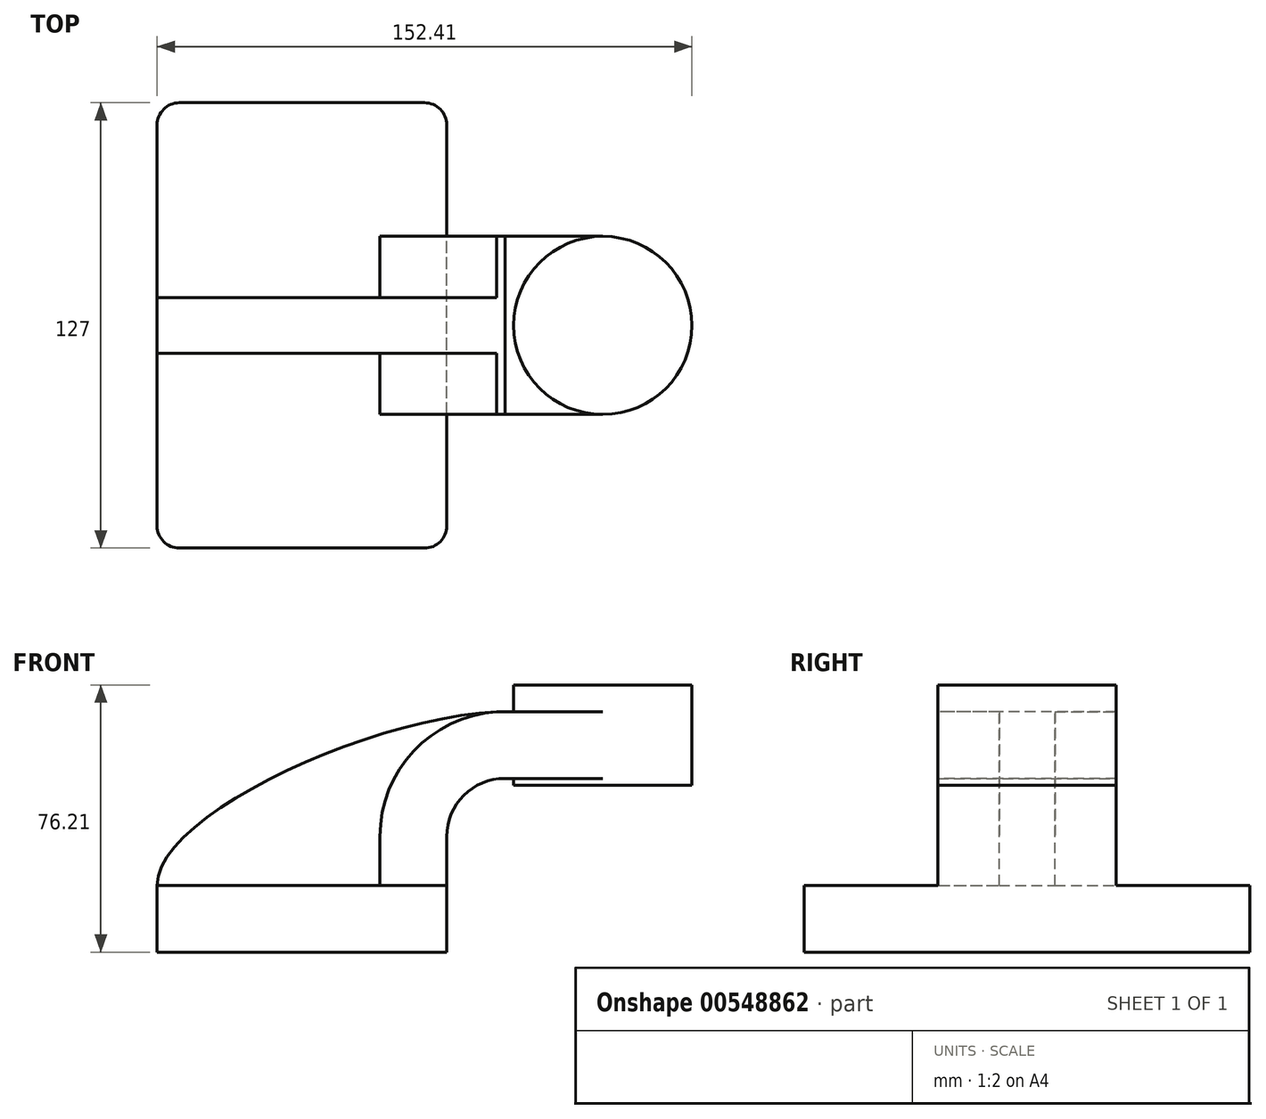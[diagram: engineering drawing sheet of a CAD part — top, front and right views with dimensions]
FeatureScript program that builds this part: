
annotation { "Feature Type Name" : "Feature", "Feature Type Description" : "" }
export const myFeature = defineFeature(function(context is Context, id is Id, definition is map)
    precondition{}
    {
        {
            var Q0;
            Q0=qCreatedBy(makeId("Front.planeOp"),FACE);
            var sketch = newSketch(context, id + "F0", { "sketchPlane" : qUnion([Q0])});
            skLineSegment(sketch, "E0.bottom", {"start": v(41.28, -9.53) * mm, "end": v(-41.28, -9.53) * mm});
            skLineSegment(sketch, "E0.top", {"start": v(41.28, 9.53) * mm, "end": v(-41.28, 9.52) * mm});
            skLineSegment(sketch, "E0.left", {"start": v(41.28, -9.53) * mm, "end": v(41.28, 9.53) * mm});
            skLineSegment(sketch, "E0.right", {"start": v(-41.28, -9.53) * mm, "end": v(-41.28, 9.52) * mm});
            skPoint(sketch, "E0.middle", {"position": v(0, 0) * mm});
            skLineSegment(sketch, "E1.left", {"start": v(3.55, 33.58) * mm, "end": v(3.55, 33.58) * mm});
            skLineSegment(sketch, "E1.right", {"start": v(63.14, 33.58) * mm, "end": v(63.14, 33.58) * mm});
            skPoint(sketch, "E1.middle", {"position": v(33.35, 33.58) * mm});
            skLineSegment(sketch, "E2", {"start": v(41.28, 9.53) * mm, "end": v(41.28, 23.44) * mm});
            skArc(sketch, "E3", {"start": v(41.28, 23.44) * mm, "mid": v(46.13, 35.15) * mm, "end": v(57.84, 40) * mm});
            skLineSegment(sketch, "E4.bottom", {"start": v(60.32, 38.1) * mm, "end": v(111.12, 38.1) * mm});
            skLineSegment(sketch, "E4.top", {"start": v(60.32, 66.67) * mm, "end": v(111.12, 66.67) * mm});
            skLineSegment(sketch, "E4.left", {"start": v(60.33, 38.1) * mm, "end": v(60.32, 66.68) * mm});
            skLineSegment(sketch, "E4.right", {"start": v(111.12, 38.1) * mm, "end": v(111.12, 66.68) * mm});
            skPoint(sketch, "E4.middle", {"position": v(85.72, 52.39) * mm});
            skLineSegment(sketch, "E5", {"start": v(57.84, 40) * mm, "end": v(85.72, 40) * mm});
            skLineSegment(sketch, "E6.0", {"start": v(57.84, 59.05) * mm, "end": v(85.72, 59.05) * mm});
            skArc(sketch, "E6.1", {"start": v(22.23, 23.44) * mm, "mid": v(32.66, 48.62) * mm, "end": v(57.84, 59.05) * mm});
            skLineSegment(sketch, "E6.2", {"start": v(22.23, 9.53) * mm, "end": v(22.23, 23.44) * mm});
            skLineSegment(sketch, "E7", {"start": v(85.72, 66.67) * mm, "end": v(85.72, 38.1) * mm});
            skFitSpline(sketch, "E8", {"points": [v(-41.28, 9.52) * mm, v(57.84, 59.05) * mm], "startDerivative": vector(-0.8, 60.38) * mm, "endDerivative": vector(110.58, 1.95) * mm});
            skSolve(sketch);
        }
        {
            var Q0;
            Q0=makeQuery(id+"F0.imprint","IMPRINT",FACE,{"disambiguationData":[TD([[makeQuery(id+"F0.imprint","IMPRINT",EDGE,{"derivedFrom":sQuery(id+"F0.wireOp",EDGE,"E0.bottom")}),-1.0]])]});
            extrude(context, id + "F1", {"entities" : qUnion([Q0]), "endBound" : BoundingType.SYMMETRIC, "depth" : 127 * mm, "offsetDistance" : 25.4 * mm});
        }
        {
            var Q0;
            {var subQ5=sQuery(id+"F0.wireOp",EDGE,"E2");Q0=makeQuery(id+"F0.imprint","IMPRINT",FACE,{"disambiguationData":[TD([[makeQuery(id+"F0.imprint","IMPRINT",EDGE,{"derivedFrom":subQ5}),1.0]])]});}
            var Q1;
            {var subQ0=sQuery(id+"F0.wireOp",EDGE,"E5");var subQ1=sQuery(id+"F0.wireOp",EDGE,"E4.left");var subQ2=makeQuery(id+"F0.imprint","INTERSECT",VERTEX,{"derivedFrom":[subQ1,subQ0]});Q1=makeQuery(id+"F0.imprint","IMPRINT",FACE,{"disambiguationData":[TD([[makeQuery(id+"F0.imprint","IMPRINT",EDGE,{"disambiguationData":[TD([[subQ2,-1.0]])],"derivedFrom":subQ1}),-1.0]])]});}
            extrude(context, id + "F2", {"entities" : qUnion([Q0, Q1]), "operationType" : NewBodyOperationType.ADD, "endBound" : BoundingType.SYMMETRIC, "depth" : 50.8 * mm, "offsetDistance" : 25.4 * mm});
        }
        {
            var Q0;
            {var subQ3=sQuery(id+"F0.wireOp",EDGE,"E6.2");Q0=makeQuery(id+"F0.imprint","IMPRINT",FACE,{"disambiguationData":[TD([[makeQuery(id+"F0.imprint","IMPRINT",EDGE,{"derivedFrom":subQ3}),1.0]])]});}
            extrude(context, id + "F3", {"entities" : qUnion([Q0]), "operationType" : NewBodyOperationType.ADD, "endBound" : BoundingType.SYMMETRIC, "depth" : 15.88 * mm, "offsetDistance" : 25.4 * mm});
        }
        {
            var Q0;
            {var subQ4=sQuery(id+"F0.wireOp",EDGE,"E4.right");Q0=makeQuery(id+"F0.imprint","IMPRINT",FACE,{"disambiguationData":[TD([[makeQuery(id+"F0.imprint","IMPRINT",EDGE,{"derivedFrom":subQ4}),1.0]])]});}
            var Q1;
            Q1=sQuery(id+"F0.wireOp",EDGE,"E7");
            revolve(context, id + "F4", {"operationType" : NewBodyOperationType.ADD, "entities" : qUnion([Q0]), "axis" : qUnion([Q1]), "revolveType" : RevolveType.FULL});
        }
        {
            var Q0;
            Q0=makeQuery(id+"F1.opExtrude","CAP_EDGE",EDGE,{"disambiguationData":[OSD([sQuery(id+"F0.wireOp",EDGE,"E0.left")])],"isStart":false});
            var Q1;
            Q1=makeQuery(id+"F1.opExtrude","CAP_EDGE",EDGE,{"disambiguationData":[OSD([sQuery(id+"F0.wireOp",EDGE,"E0.right")])],"isStart":false});
            var Q2;
            Q2=makeQuery(id+"F1.opExtrude","CAP_EDGE",EDGE,{"disambiguationData":[OSD([sQuery(id+"F0.wireOp",EDGE,"E0.left")])],"isStart":true});
            var Q3;
            Q3=makeQuery(id+"F1.opExtrude","CAP_EDGE",EDGE,{"disambiguationData":[OSD([sQuery(id+"F0.wireOp",EDGE,"E0.right")])],"isStart":true});
            fillet(context, id + "F5", {"entities" : qUnion([Q0, Q1, Q2, Q3]), "radius" : 6.35 * mm, "tangentPropagation" : true, "allowEdgeOverflow" : false});
        }
    });
